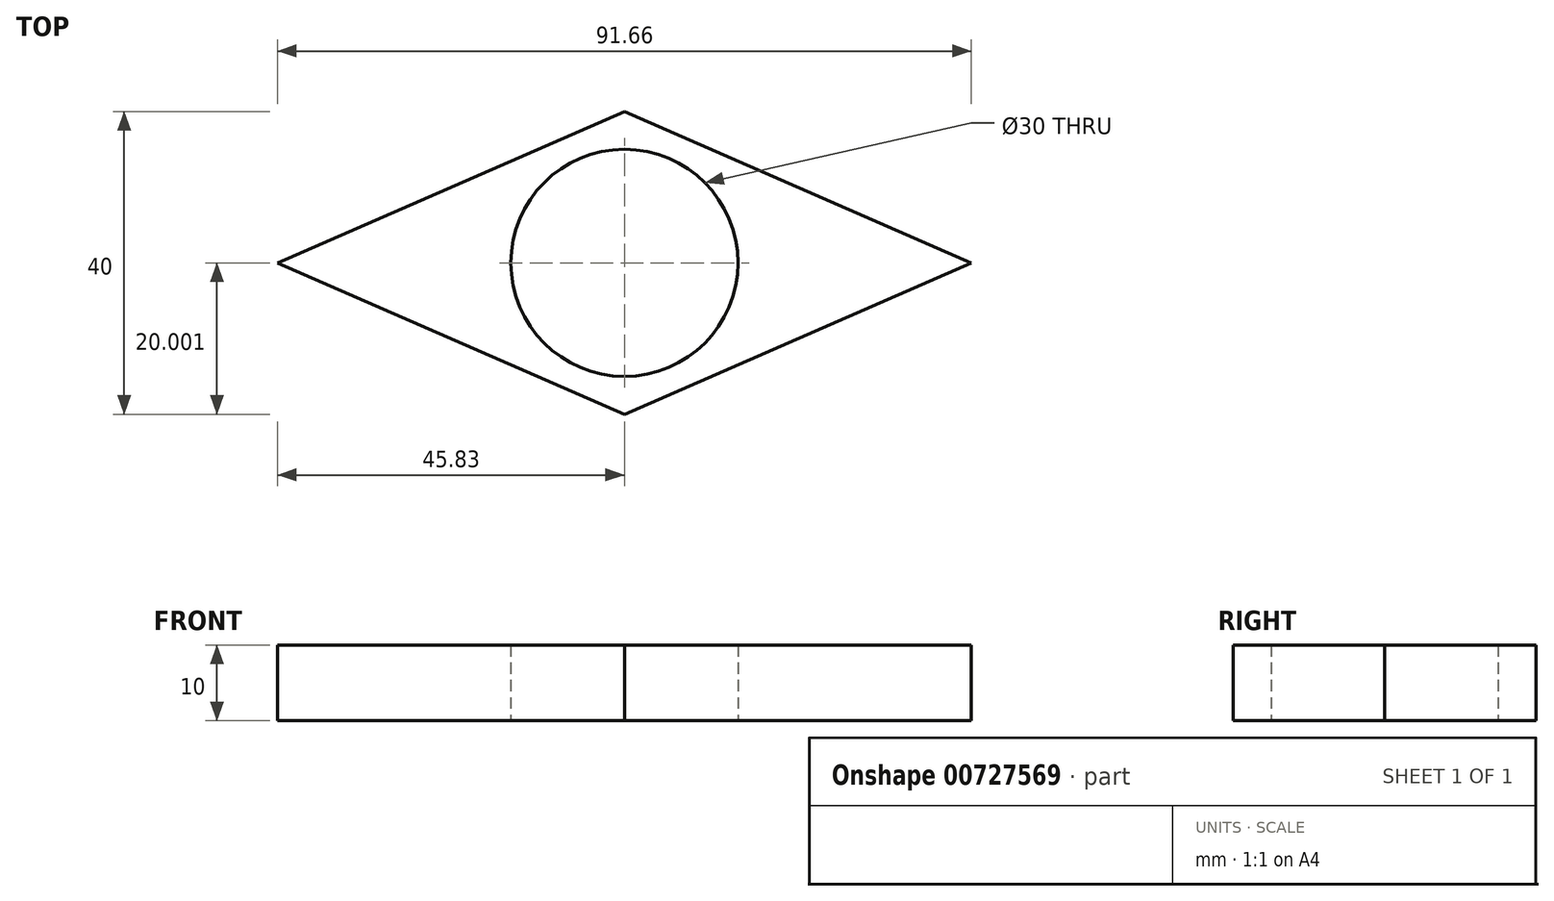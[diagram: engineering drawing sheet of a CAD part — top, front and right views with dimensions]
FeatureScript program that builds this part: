
annotation { "Feature Type Name" : "Feature", "Feature Type Description" : "" }
export const myFeature = defineFeature(function(context is Context, id is Id, definition is map)
    precondition{}
    {
        {
            var Q0;
            Q0=qCreatedBy(makeId("Top.planeOp"),FACE);
            var sketch = newSketch(context, id + "F0", { "sketchPlane" : qUnion([Q0])});
            skLineSegment(sketch, "E0", {"start": v(-981.62, 224.65) * mm, "end": v(-1027.45, 244.65) * mm});
            skLineSegment(sketch, "E1", {"start": v(-1027.45, 244.65) * mm, "end": v(-981.62, 264.65) * mm});
            skLineSegment(sketch, "E2", {"start": v(-981.62, 224.65) * mm, "end": v(-935.8, 244.65) * mm});
            skLineSegment(sketch, "E3", {"start": v(-935.8, 244.65) * mm, "end": v(-981.62, 264.65) * mm});
            skPoint(sketch, "E4.start.orphan", {"position": v(-981.62, 229.65) * mm});
            skPoint(sketch, "E5.center.orphan", {"position": v(-981.62, 244.65) * mm});
            skSolve(sketch);
        }
        {
            var Q0;
            Q0=makeQuery(id+"F0.imprint","IMPRINT",FACE,{"disambiguationData":[TD([[makeQuery(id+"F0.imprint","IMPRINT",EDGE,{"derivedFrom":sQuery(id+"F0.wireOp",EDGE,"E0")}),-1.0]])]});
            extrude(context, id + "F1", {"entities" : qUnion([Q0]), "depth" : 10 * mm, "offsetDistance" : 25 * mm});
        }
        {
            var Q0;
            Q0=makeQuery(id+"F1.opExtrude","CAP_FACE",FACE,{"disambiguationData":[OSD([sQuery(id+"F0.wireOp",EDGE,"E0"),sQuery(id+"F0.wireOp",EDGE,"E1"),sQuery(id+"F0.wireOp",EDGE,"E2"),sQuery(id+"F0.wireOp",EDGE,"E3")])],"isStart":true});
            var sketch = newSketch(context, id + "F2", { "sketchPlane" : qUnion([Q0])});
            skCircle(sketch, "E6", {"center": v(-981.62, -244.65) * mm, "radius": 15 * mm});
            skSolve(sketch);
        }
        {
            var Q0;
            Q0=makeQuery(id+"F2.imprint","IMPRINT",FACE,{"disambiguationData":[TD([[makeQuery(id+"F2.imprint","IMPRINT",EDGE,{"derivedFrom":sQuery(id+"F2.wireOp",EDGE,"E6")}),1.0]])]});
            extrude(context, id + "F3", {"entities" : qUnion([Q0]), "operationType" : NewBodyOperationType.REMOVE, "endBound" : BoundingType.THROUGH_ALL, "oppositeDirection" : true, "depth" : 25 * mm, "offsetDistance" : 25 * mm});
        }
    });
